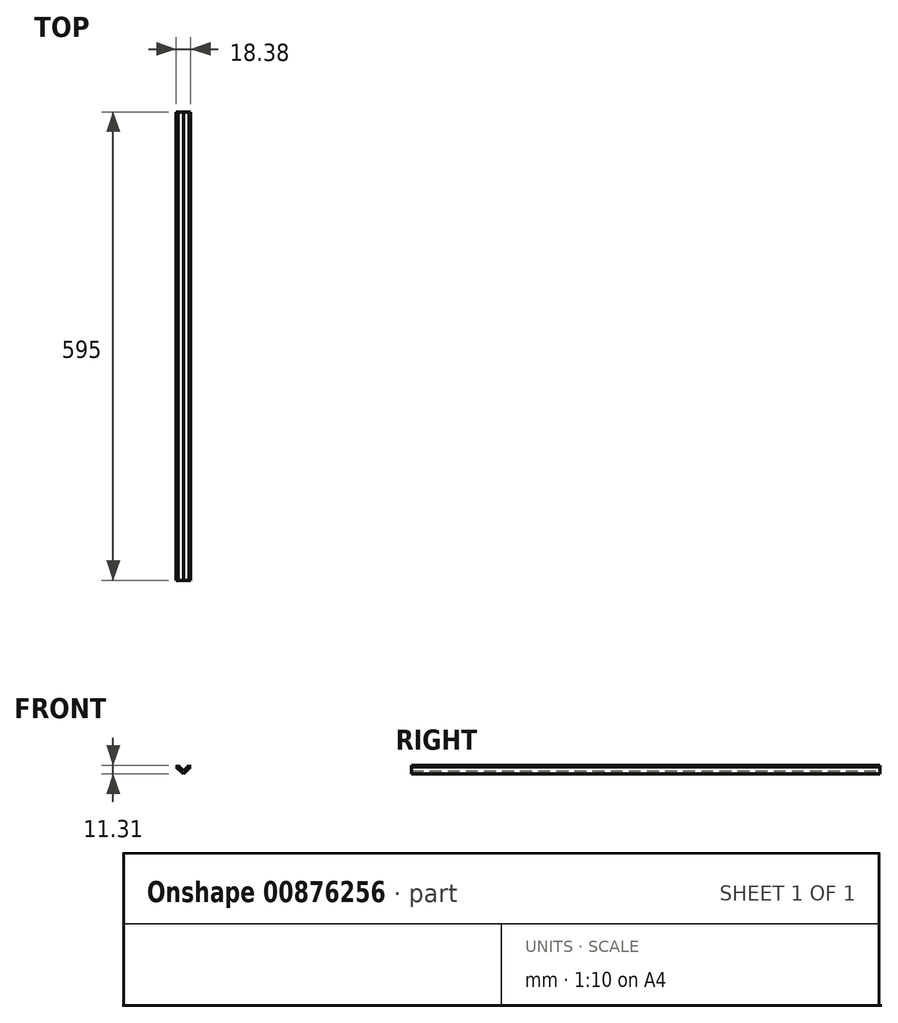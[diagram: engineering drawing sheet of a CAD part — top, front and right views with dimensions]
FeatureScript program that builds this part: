
annotation { "Feature Type Name" : "Feature", "Feature Type Description" : "" }
export const myFeature = defineFeature(function(context is Context, id is Id, definition is map)
    precondition{}
    {
        {
            var Q0;
            Q0=qCreatedBy(makeId("Front.planeOp"),FACE);
            var sketch = newSketch(context, id + "F0", { "sketchPlane" : qUnion([Q0])});
            skLineSegment(sketch, "E0", {"start": v(0, 0) * mm, "end": v(-7.07, 7.07) * mm});
            skLineSegment(sketch, "E1", {"start": v(-7.07, 7.07) * mm, "end": v(-9.2, 4.95) * mm});
            skLineSegment(sketch, "E2", {"start": v(-9.2, 4.95) * mm, "end": v(0, -4.24) * mm});
            skLineSegment(sketch, "E3", {"start": v(0, -4.24) * mm, "end": v(0, 0) * mm, "construction": true});
            skLineSegment(sketch, "E4.MirrorCS", {"start": v(0, 0) * mm, "end": v(7.07, 7.07) * mm});
            skLineSegment(sketch, "E5.MirrorCS", {"start": v(7.07, 7.07) * mm, "end": v(9.2, 4.95) * mm});
            skLineSegment(sketch, "E6.MirrorCS", {"start": v(9.2, 4.95) * mm, "end": v(0, -4.24) * mm});
            skSolve(sketch);
        }
        {
            var Q0;
            Q0=makeQuery(id+"F0.imprint","IMPRINT",FACE,{"disambiguationData":[TD([[makeQuery(id+"F0.imprint","IMPRINT",EDGE,{"derivedFrom":sQuery(id+"F0.wireOp",EDGE,"E0")}),1.0]])]});
            extrude(context, id + "F1", {"entities" : qUnion([Q0]), "depth" : 580 * mm + 15 * mm, "offsetDistance" : 25.4 * mm});
        }
    });
